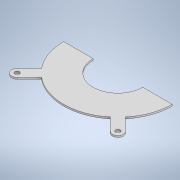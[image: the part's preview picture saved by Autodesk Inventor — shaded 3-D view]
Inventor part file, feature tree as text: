
AUTODESK INVENTOR PART (.ipt)
format: ipt  version: 2022.2 (Build 262287010, 287A)  size: 122,880 bytes
history: native  units: in
note: dims shown in document units (in); Inventor stores cm internally (conversion verified against a paired STEP export)
features: extrude x1, sketch x1
ambient origin geometry x8: Origin, YZ Plane, XZ Plane, XY Plane, X Axis, Y Axis, Z Axis, Center Point
bodies: Body1 (feature_tree)
feature tree (2):
  extrude  "Extrusión2"  Depth=0.0787in
  sketch  "Boceto1"  dims[d9=0.2165in d11=0.2165in d12=0.0787in d13=0.0in]
